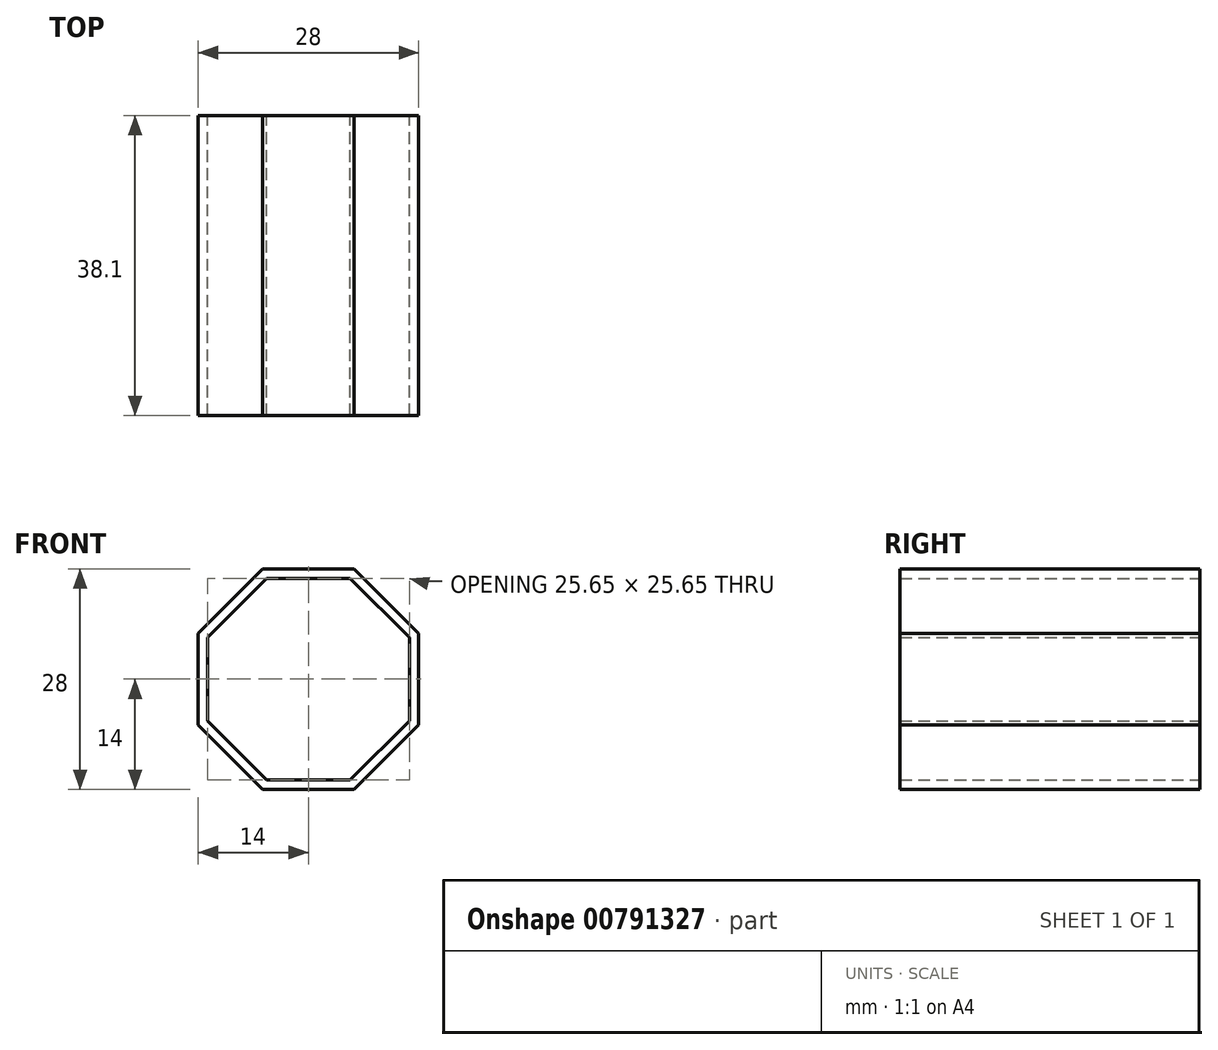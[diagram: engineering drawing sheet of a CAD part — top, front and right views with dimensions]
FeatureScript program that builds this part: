
annotation { "Feature Type Name" : "Feature", "Feature Type Description" : "" }
export const myFeature = defineFeature(function(context is Context, id is Id, definition is map)
    precondition{}
    {
        {
            var Q0;
            Q0=qCreatedBy(makeId("Front.planeOp"),FACE);
            var sketch = newSketch(context, id + "F0", { "sketchPlane" : qUnion([Q0])});
            skPoint(sketch, "E0", {"position": v(0, 14) * mm});
            skPoint(sketch, "E1", {"position": v(0, -14) * mm});
            skPoint(sketch, "E2", {"position": v(-14, 0) * mm});
            skPoint(sketch, "E3", {"position": v(14, 0) * mm});
            skLineSegment(sketch, "E4", {"start": v(0, 0) * mm, "end": v(-9.9, 9.9) * mm});
            skLineSegment(sketch, "E5", {"start": v(-9.9, -9.9) * mm, "end": v(0, 0) * mm});
            skLineSegment(sketch, "E6", {"start": v(9.9, 9.9) * mm, "end": v(0, 0) * mm});
            skLineSegment(sketch, "E7", {"start": v(9.9, -9.9) * mm, "end": v(0, 0) * mm});
            skLineSegment(sketch, "E8", {"start": v(0, 14) * mm, "end": v(0, 0) * mm, "construction": true});
            skPoint(sketch, "E9", {"position": v(-9.9, 9.9) * mm});
            skPoint(sketch, "E10", {"position": v(-9.9, -9.9) * mm});
            skPoint(sketch, "E11", {"position": v(9.9, -9.9) * mm});
            skPoint(sketch, "E12", {"position": v(9.9, 9.9) * mm});
            skLineSegment(sketch, "E13", {"start": v(14, 5.8) * mm, "end": v(14, -5.8) * mm});
            skLineSegment(sketch, "E14", {"start": v(-5.8, -14) * mm, "end": v(5.8, -14) * mm});
            skLineSegment(sketch, "E15", {"start": v(-14, 5.8) * mm, "end": v(-5.8, 14) * mm});
            skLineSegment(sketch, "E16", {"start": v(5.8, 14) * mm, "end": v(14, 5.8) * mm});
            skLineSegment(sketch, "E17", {"start": v(14, -5.8) * mm, "end": v(5.8, -14) * mm});
            skLineSegment(sketch, "E18", {"start": v(-14, -5.8) * mm, "end": v(-5.8, -14) * mm});
            skLineSegment(sketch, "E19.trimOffspring", {"start": v(-5.8, 14) * mm, "end": v(5.8, 14) * mm});
            skLineSegment(sketch, "E20.trimOffspring", {"start": v(-14, 5.8) * mm, "end": v(-14, -5.8) * mm});
            skPoint(sketch, "E21.start.orphan", {"position": v(-15.18, 14) * mm});
            skPoint(sketch, "E22.start.orphan", {"position": v(-14, 16.34) * mm});
            skPoint(sketch, "E23.orphan", {"position": v(-15.11, -14) * mm});
            skPoint(sketch, "E24.orphan", {"position": v(14, 17.3) * mm});
            skPoint(sketch, "E25.orphan", {"position": v(19.8, 0) * mm});
            skPoint(sketch, "E26", {"position": v(0, 0) * mm});
            skPoint(sketch, "E27", {"position": v(-14, 5.8) * mm});
            skPoint(sketch, "E28", {"position": v(-5.8, 14) * mm});
            skPoint(sketch, "E29", {"position": v(5.8, 14) * mm});
            skPoint(sketch, "E30", {"position": v(14, 5.8) * mm});
            skPoint(sketch, "E31", {"position": v(14, -5.8) * mm});
            skPoint(sketch, "E32", {"position": v(5.8, -14) * mm});
            skPoint(sketch, "E33", {"position": v(-5.8, -14) * mm});
            skPoint(sketch, "E34", {"position": v(-14, -5.8) * mm});
            skLineSegment(sketch, "E35", {"start": v(0, 0) * mm, "end": v(5.8, 14) * mm, "construction": true});
            skLineSegment(sketch, "E36", {"start": v(0, 0) * mm, "end": v(14, 5.8) * mm, "construction": true});
            skLineSegment(sketch, "E37", {"start": v(0, 0) * mm, "end": v(14, -5.8) * mm, "construction": true});
            skLineSegment(sketch, "E38", {"start": v(0, 0) * mm, "end": v(5.8, -14) * mm, "construction": true});
            skLineSegment(sketch, "E39", {"start": v(0, 0) * mm, "end": v(0, -14) * mm, "construction": true});
            skLineSegment(sketch, "E40.MirrorCS", {"start": v(0, 0) * mm, "end": v(-5.8, 14) * mm, "construction": true});
            skLineSegment(sketch, "E41.MirrorCS", {"start": v(0, 0) * mm, "end": v(-14, 5.8) * mm, "construction": true});
            skLineSegment(sketch, "E42.MirrorCS", {"start": v(0, 0) * mm, "end": v(-14, -5.8) * mm, "construction": true});
            skLineSegment(sketch, "E43.MirrorCS", {"start": v(0, 0) * mm, "end": v(-5.8, -14) * mm, "construction": true});
            skPoint(sketch, "E44", {"position": v(-12.82, 5.31) * mm});
            skLineSegment(sketch, "E45", {"start": v(-12.82, 5.31) * mm, "end": v(-12.82, -5.31) * mm});
            skLineSegment(sketch, "E46", {"start": v(-12.82, -5.31) * mm, "end": v(-5.31, -12.82) * mm});
            skLineSegment(sketch, "E47", {"start": v(-5.31, -12.82) * mm, "end": v(5.31, -12.82) * mm});
            skLineSegment(sketch, "E48", {"start": v(5.31, -12.82) * mm, "end": v(12.82, -5.31) * mm});
            skLineSegment(sketch, "E49", {"start": v(12.82, -5.31) * mm, "end": v(12.82, 5.31) * mm});
            skLineSegment(sketch, "E50", {"start": v(12.82, 5.31) * mm, "end": v(5.31, 12.82) * mm});
            skLineSegment(sketch, "E51", {"start": v(5.31, 12.82) * mm, "end": v(-5.31, 12.82) * mm});
            skLineSegment(sketch, "E52", {"start": v(-5.31, 12.82) * mm, "end": v(-12.82, 5.31) * mm});
            skSolve(sketch);
        }
        {
            var Q0;
            {var subQ3=sQuery(id+"F0.wireOp",EDGE,"E19.trimOffspring");Q0=makeQuery(id+"F0.imprint","IMPRINT",FACE,{"disambiguationData":[TD([[makeQuery(id+"F0.imprint","IMPRINT",EDGE,{"derivedFrom":subQ3}),-1.0]])]});}
            var Q1;
            {var subQ3=sQuery(id+"F0.wireOp",EDGE,"E20.trimOffspring");Q1=makeQuery(id+"F0.imprint","IMPRINT",FACE,{"disambiguationData":[TD([[makeQuery(id+"F0.imprint","IMPRINT",EDGE,{"derivedFrom":subQ3}),1.0]])]});}
            var Q2;
            {var subQ3=sQuery(id+"F0.wireOp",EDGE,"E13");Q2=makeQuery(id+"F0.imprint","IMPRINT",FACE,{"disambiguationData":[TD([[makeQuery(id+"F0.imprint","IMPRINT",EDGE,{"derivedFrom":subQ3}),-1.0]])]});}
            var Q3;
            {var subQ3=sQuery(id+"F0.wireOp",EDGE,"E14");Q3=makeQuery(id+"F0.imprint","IMPRINT",FACE,{"disambiguationData":[TD([[makeQuery(id+"F0.imprint","IMPRINT",EDGE,{"derivedFrom":subQ3}),1.0]])]});}
            extrude(context, id + "F1", {"entities" : qUnion([Q0, Q1, Q2, Q3]), "endBound" : BoundingType.SYMMETRIC, "depth" : 38.1 * mm, "offsetDistance" : 25.4 * mm});
        }
    });
